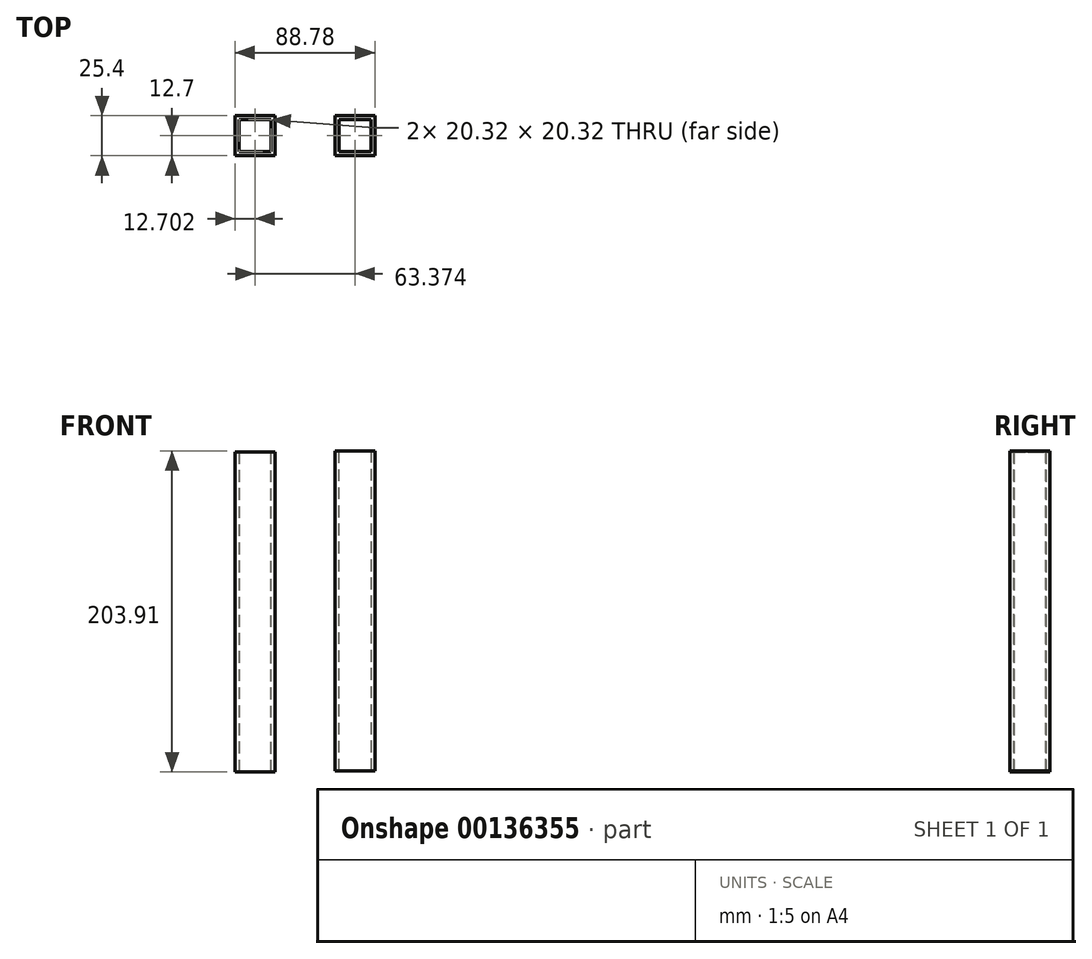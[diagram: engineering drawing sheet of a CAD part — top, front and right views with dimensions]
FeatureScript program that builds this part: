
annotation { "Feature Type Name" : "Feature", "Feature Type Description" : "" }
export const myFeature = defineFeature(function(context is Context, id is Id, definition is map)
    precondition{}
    {
        {
            var Q0;
            Q0=qCreatedBy(makeId("Front.planeOp"),FACE);
            var sketch = newSketch(context, id + "F0", { "sketchPlane" : qUnion([Q0])});
            skLineSegment(sketch, "E0", {"start": v(-39.25, 98.96) * mm, "end": v(-39.25, -104.24) * mm});
            skLineSegment(sketch, "E1", {"start": v(-39.25, -104.24) * mm, "end": v(-13.85, -104.24) * mm});
            skLineSegment(sketch, "E2", {"start": v(-39.25, 98.96) * mm, "end": v(-13.85, 98.96) * mm});
            skLineSegment(sketch, "E3", {"start": v(-13.85, -104.24) * mm, "end": v(-13.85, 98.96) * mm});
            skLineSegment(sketch, "E4", {"start": v(24.13, -103.53) * mm, "end": v(49.53, -103.53) * mm});
            skLineSegment(sketch, "E5", {"start": v(24.13, -103.53) * mm, "end": v(24.13, 99.67) * mm});
            skLineSegment(sketch, "E6", {"start": v(24.13, 99.67) * mm, "end": v(49.53, 99.67) * mm});
            skLineSegment(sketch, "E7", {"start": v(49.53, 99.67) * mm, "end": v(49.53, -103.53) * mm});
            skSolve(sketch);
        }
        {
            var Q0;
            Q0=makeQuery(id+"F0.imprint","IMPRINT",FACE,{"disambiguationData":[TD([[makeQuery(id+"F0.imprint","IMPRINT",EDGE,{"derivedFrom":sQuery(id+"F0.wireOp",EDGE,"E4")}),1.0]])]});
            var Q1;
            Q1=makeQuery(id+"F0.imprint","IMPRINT",FACE,{"disambiguationData":[TD([[makeQuery(id+"F0.imprint","IMPRINT",EDGE,{"derivedFrom":sQuery(id+"F0.wireOp",EDGE,"E0")}),1.0]])]});
            extrude(context, id + "F1", {"entities" : qUnion([Q0, Q1]), "depth" : 25.4 * mm});
        }
        {
            var Q0;
            Q0=makeQuery(id+"F1.opExtrude","SWEPT_FACE",FACE,{"disambiguationData":[OSD([sQuery(id+"F0.wireOp",EDGE,"E2")])]});
            var Q1;
            Q1=makeQuery(id+"F1.opExtrude","SWEPT_FACE",FACE,{"disambiguationData":[OSD([sQuery(id+"F0.wireOp",EDGE,"E6")])]});
            var Q2;
            Q2=makeQuery(id+"F1.opExtrude","SWEPT_FACE",FACE,{"disambiguationData":[OSD([sQuery(id+"F0.wireOp",EDGE,"E1")])]});
            var Q3;
            Q3=makeQuery(id+"F1.opExtrude","SWEPT_FACE",FACE,{"disambiguationData":[OSD([sQuery(id+"F0.wireOp",EDGE,"E4")])]});
            shell(context, id + "F2", {"entities" : qUnion([Q0, Q1, Q2, Q3]), "thickness" : 2.54 * mm});
        }
    });
